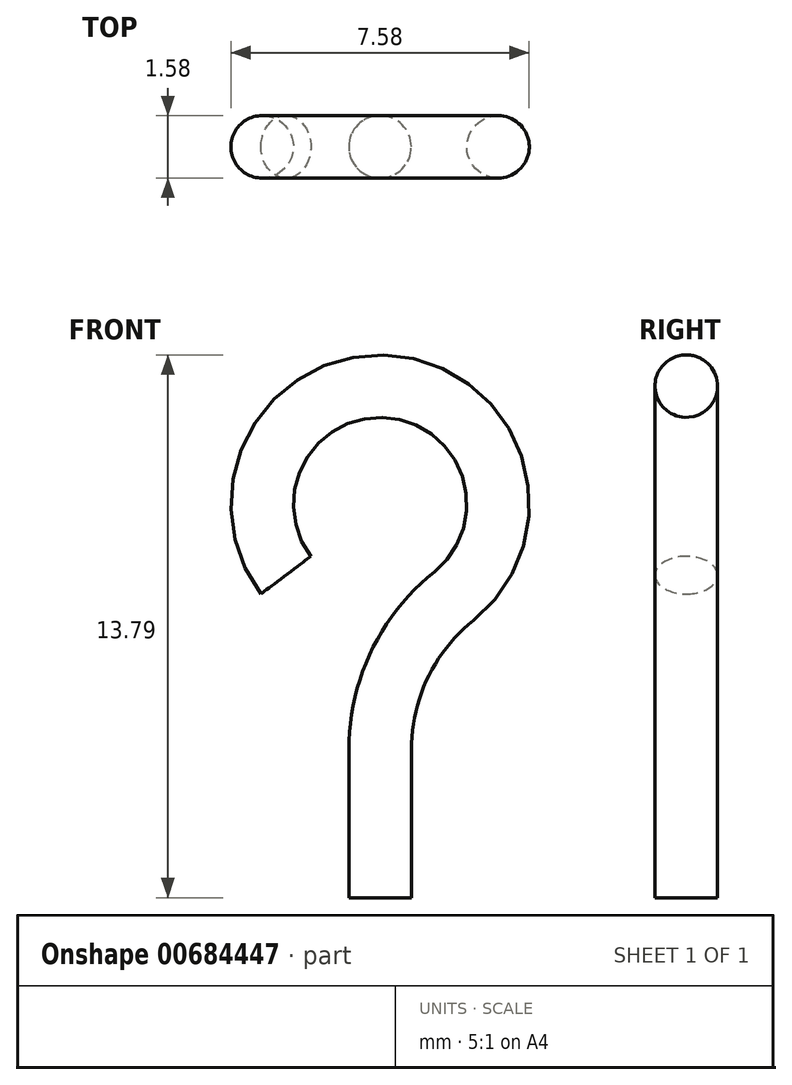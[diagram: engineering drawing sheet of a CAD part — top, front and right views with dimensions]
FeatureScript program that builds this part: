
annotation { "Feature Type Name" : "Feature", "Feature Type Description" : "" }
export const myFeature = defineFeature(function(context is Context, id is Id, definition is map)
    precondition{}
    {
        {
            var Q0;
            Q0=qCreatedBy(makeId("Front.planeOp"),FACE);
            var sketch = newSketch(context, id + "F0", { "sketchPlane" : qUnion([Q0])});
            skLineSegment(sketch, "E0", {"start": v(0, -6.24) * mm, "end": v(0, -10) * mm});
            skArc(sketch, "E1", {"start": v(1.88, -2.34) * mm, "mid": v(0.37, 2.98) * mm, "end": v(-2.4, -1.8) * mm});
            skLineSegment(sketch, "E2", {"start": v(0, 0) * mm, "end": v(-2.4, -1.8) * mm});
            skArc(sketch, "E3.filletArc", {"start": v(1.88, -2.34) * mm, "mid": v(0.5, -4.08) * mm, "end": v(0, -6.24) * mm});
            skSolve(sketch);
        }
        {
            var Q0;
            Q0=qCreatedBy(makeId("Top.planeOp"),FACE);
            cPlane(context, id + "F1", {"entities" : qUnion([Q0]), "cplaneType" : CPlaneType.OFFSET, "offset" : 10 * mm, "oppositeDirection" : true, "width" : 152.4 * mm, "height" : 152.4 * mm});
        }
        {
            var Q0;
            Q0=qCreatedBy(id+"F1.planeOp",FACE);
            var sketch = newSketch(context, id + "F2", { "sketchPlane" : qUnion([Q0])});
            skCircle(sketch, "E4", {"center": v(0, 0) * mm, "radius": 0.8 * mm});
            skSolve(sketch);
        }
        {
            var Q0;
            Q0=makeQuery(id+"F2.imprint","IMPRINT",FACE,{"disambiguationData":[TD([[makeQuery(id+"F2.imprint","IMPRINT",EDGE,{"derivedFrom":sQuery(id+"F2.wireOp",EDGE,"E4")}),1.0]])]});
            var Q1;
            Q1=sQuery(id+"F0.wireOp",EDGE,"E0");
            var Q2;
            Q2=sQuery(id+"F0.wireOp",EDGE,"E3.filletArc");
            var Q3;
            Q3=sQuery(id+"F0.wireOp",EDGE,"E1");
            sweep(context, id + "F3", {"profiles" : qUnion([Q0]), "path" : qUnion([Q1, Q2, Q3])});
        }
    });
